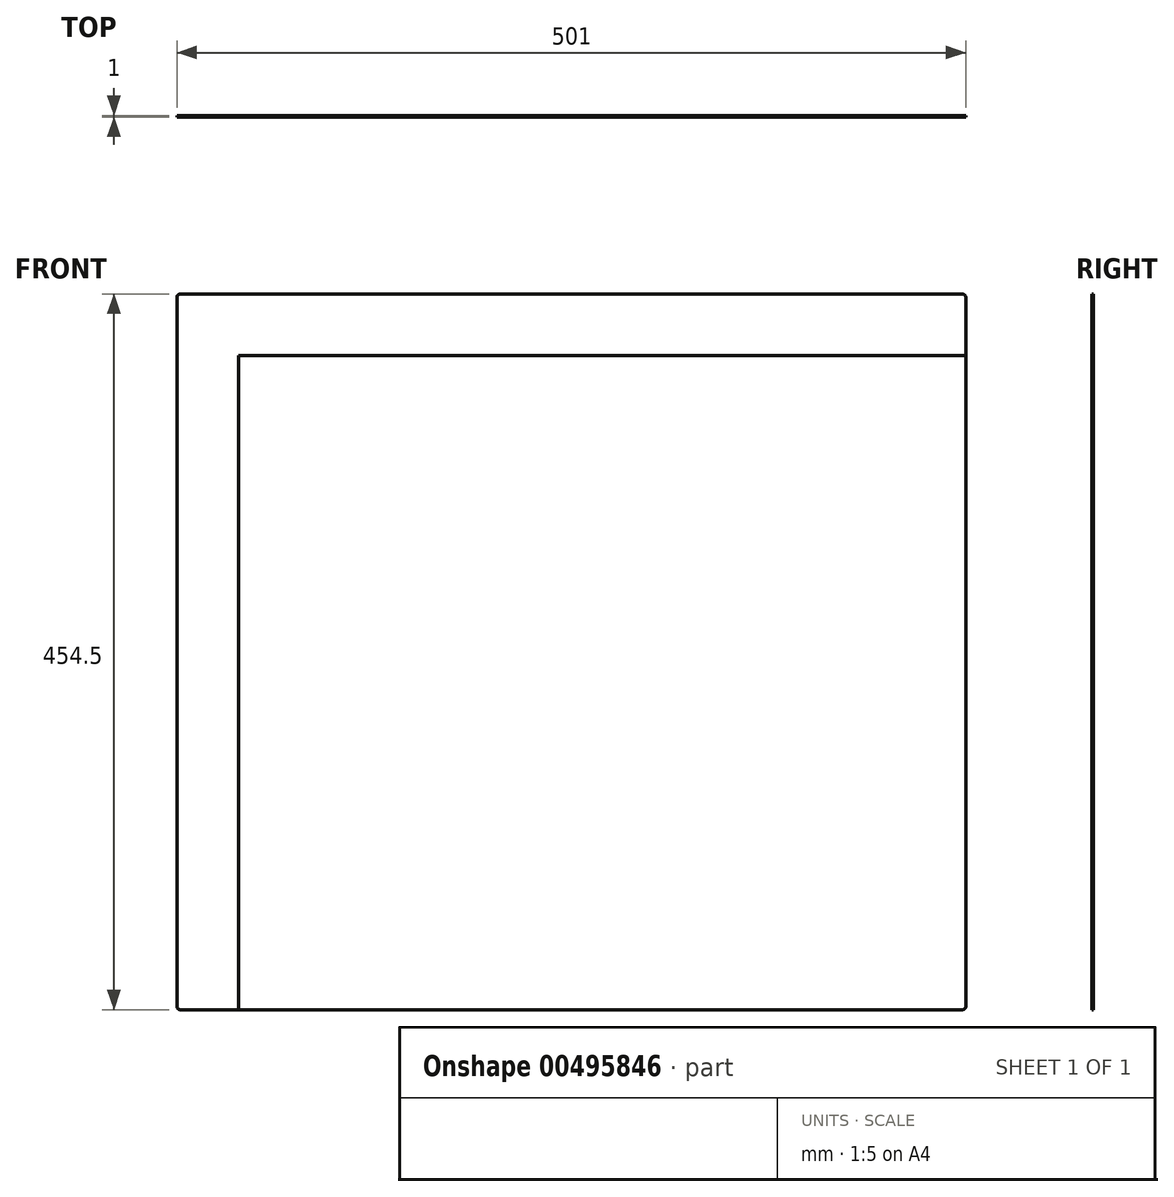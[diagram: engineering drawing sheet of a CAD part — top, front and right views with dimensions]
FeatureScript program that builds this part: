
annotation { "Feature Type Name" : "Feature", "Feature Type Description" : "" }
export const myFeature = defineFeature(function(context is Context, id is Id, definition is map)
    precondition{}
    {
        {
            var Q0;
            Q0=qCreatedBy(makeId("Front.planeOp"),FACE);
            var sketch = newSketch(context, id + "F0", { "sketchPlane" : qUnion([Q0])});
            skLineSegment(sketch, "E0.bottom", {"start": v(248.5, 227.25) * mm, "end": v(-248.5, 227.25) * mm});
            skLineSegment(sketch, "E0.top", {"start": v(248.5, -227.25) * mm, "end": v(-248.5, -227.25) * mm});
            skLineSegment(sketch, "E0.left", {"start": v(250.5, 225.25) * mm, "end": v(250.5, -225.25) * mm});
            skLineSegment(sketch, "E0.right", {"start": v(-250.5, 225.25) * mm, "end": v(-250.5, -225.25) * mm});
            skPoint(sketch, "E0.middle", {"position": v(0, 0) * mm});
            skLineSegment(sketch, "E1", {"start": v(-211.5, -227.25) * mm, "end": v(-211.5, 188.25) * mm});
            skLineSegment(sketch, "E2", {"start": v(-211.5, 188.25) * mm, "end": v(250.5, 188.25) * mm});
            skPoint(sketch, "E3.visualSharp", {"position": v(-250.5, 227.25) * mm});
            skArc(sketch, "E3.filletArc", {"start": v(-248.5, 227.25) * mm, "mid": v(-249.91, 226.66) * mm, "end": v(-250.5, 225.25) * mm});
            skPoint(sketch, "E4.visualSharp", {"position": v(250.5, 227.25) * mm});
            skArc(sketch, "E4.filletArc", {"start": v(250.5, 225.25) * mm, "mid": v(249.91, 226.66) * mm, "end": v(248.5, 227.25) * mm});
            skPoint(sketch, "E5.visualSharp", {"position": v(250.5, -227.25) * mm});
            skArc(sketch, "E5.filletArc", {"start": v(248.5, -227.25) * mm, "mid": v(249.91, -226.66) * mm, "end": v(250.5, -225.25) * mm});
            skPoint(sketch, "E6.visualSharp", {"position": v(-250.5, -227.25) * mm});
            skArc(sketch, "E6.filletArc", {"start": v(-250.5, -225.25) * mm, "mid": v(-249.91, -226.66) * mm, "end": v(-248.5, -227.25) * mm});
            skSolve(sketch);
        }
        {
            var Q0;
            {var subQ1=sQuery(id+"F0.wireOp",EDGE,"E1");Q0=makeQuery(id+"F0.imprint","IMPRINT",FACE,{"disambiguationData":[TD([[makeQuery(id+"F0.imprint","IMPRINT",EDGE,{"derivedFrom":subQ1}),-1.0]])]});}
            extrude(context, id + "F1", {"entities" : qUnion([Q0]), "depth" : 1 * mm});
        }
        {
            var Q0;
            Q0=makeQuery(id+"F0.imprint","IMPRINT",FACE,{"disambiguationData":[TD([[makeQuery(id+"F0.imprint","IMPRINT",EDGE,{"derivedFrom":sQuery(id+"F0.wireOp",EDGE,"E0.bottom")}),1.0]])]});
            extrude(context, id + "F2", {"entities" : qUnion([Q0]), "depth" : 1 * mm});
        }
    });
